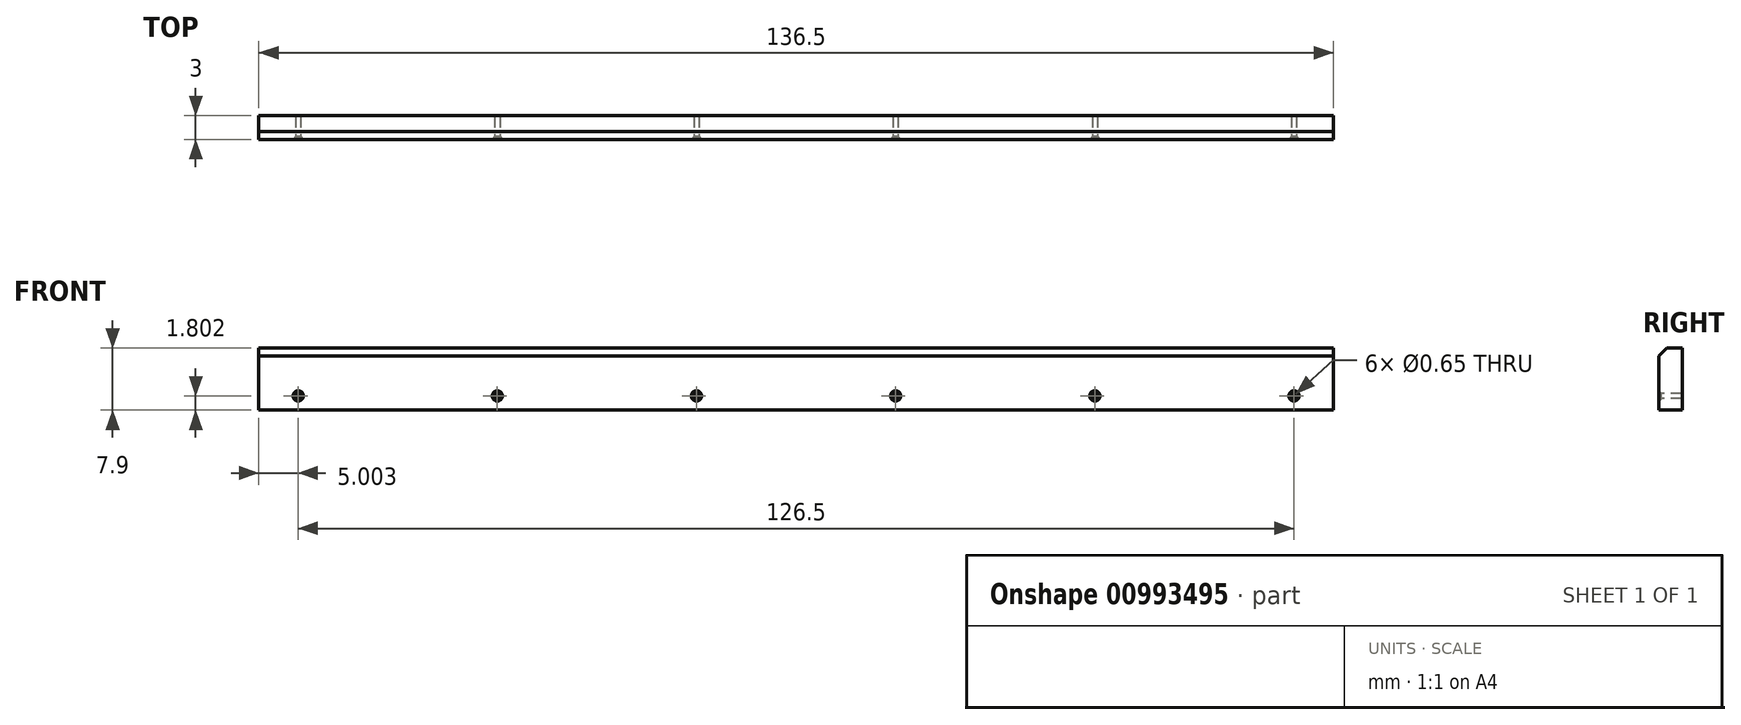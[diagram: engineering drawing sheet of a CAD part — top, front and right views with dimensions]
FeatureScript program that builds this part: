
annotation { "Feature Type Name" : "Feature", "Feature Type Description" : "" }
export const myFeature = defineFeature(function(context is Context, id is Id, definition is map)
    precondition{}
    {
        {
            var Q0;
            Q0=qCreatedBy(makeId("Front.planeOp"),FACE);
            var sketch = newSketch(context, id + "F0", { "sketchPlane" : qUnion([Q0])});
            skLineSegment(sketch, "E0.bottom", {"start": v(-73.38, 15.44) * mm, "end": v(63.12, 15.44) * mm});
            skLineSegment(sketch, "E0.top", {"start": v(-73.38, 7.54) * mm, "end": v(63.12, 7.54) * mm});
            skLineSegment(sketch, "E0.left", {"start": v(-73.38, 15.44) * mm, "end": v(-73.38, 7.54) * mm});
            skLineSegment(sketch, "E0.right", {"start": v(63.12, 15.44) * mm, "end": v(63.12, 7.54) * mm});
            skPoint(sketch, "E1", {"position": v(-68.38, 9.34) * mm});
            skPoint(sketch, "E2", {"position": v(-43.08, 9.34) * mm});
            skPoint(sketch, "E3", {"position": v(-17.78, 9.34) * mm});
            skPoint(sketch, "E4", {"position": v(7.52, 9.34) * mm});
            skPoint(sketch, "E5", {"position": v(32.82, 9.34) * mm});
            skPoint(sketch, "E6", {"position": v(58.12, 9.34) * mm});
            skSolve(sketch);
        }
        {
            var Q0;
            Q0=makeQuery(id+"F0.imprint","IMPRINT",FACE,{"disambiguationData":[TD([[makeQuery(id+"F0.imprint","IMPRINT",EDGE,{"derivedFrom":sQuery(id+"F0.wireOp",EDGE,"E0.bottom")}),-1.0]])]});
            extrude(context, id + "F1", {"entities" : qUnion([Q0]), "oppositeDirection" : true, "depth" : 3 * mm, "offsetDistance" : 25 * mm});
        }
        {
            var Q0;
            Q0=sQuery(id+"F0.wireOp",VERTEX,"E6");
            var Q1;
            Q1=sQuery(id+"F0.wireOp",VERTEX,"E5");
            var Q2;
            Q2=sQuery(id+"F0.wireOp",VERTEX,"E4");
            var Q3;
            Q3=sQuery(id+"F0.wireOp",VERTEX,"E3");
            var Q4;
            Q4=sQuery(id+"F0.wireOp",VERTEX,"E2");
            var Q5;
            Q5=sQuery(id+"F0.wireOp",VERTEX,"E1");
            var Q6;
            Q6=makeQuery(id+"F1.opExtrude","SWEPT_BODY",BODY,{"disambiguationData":[OSD([sQuery(id+"F0.wireOp",EDGE,"E0.bottom"),sQuery(id+"F0.wireOp",EDGE,"E0.top"),sQuery(id+"F0.wireOp",EDGE,"E0.left"),sQuery(id+"F0.wireOp",EDGE,"E0.right")])]});
            hole(context, id + "F2", {"style" : HoleStyle.C_SINK, "endStyle" : HoleEndStyle.THROUGH, "holeDiameter" : 0.65 * mm, "cSinkDiameter" : 1.3 * mm, "cSinkAngle" : 90 * degree, "majorDiameter" : 5 * mm, "isTappedThrough" : true, "tappedDepth" : 12 * mm, "tapClearance" : 3, "locations" : qUnion([Q0, Q1, Q2, Q3, Q4, Q5]), "scope" : qUnion([Q6])});
        }
        {
            var Q0;
            Q0=makeQuery(id+"F1.opExtrude","CAP_EDGE",EDGE,{"disambiguationData":[OSD([sQuery(id+"F0.wireOp",EDGE,"E0.bottom")])],"isStart":true});
            chamfer(context, id + "F3", {"entities" : qUnion([Q0]), "width" : 1 * mm, "tangentPropagation" : true});
        }
    });
